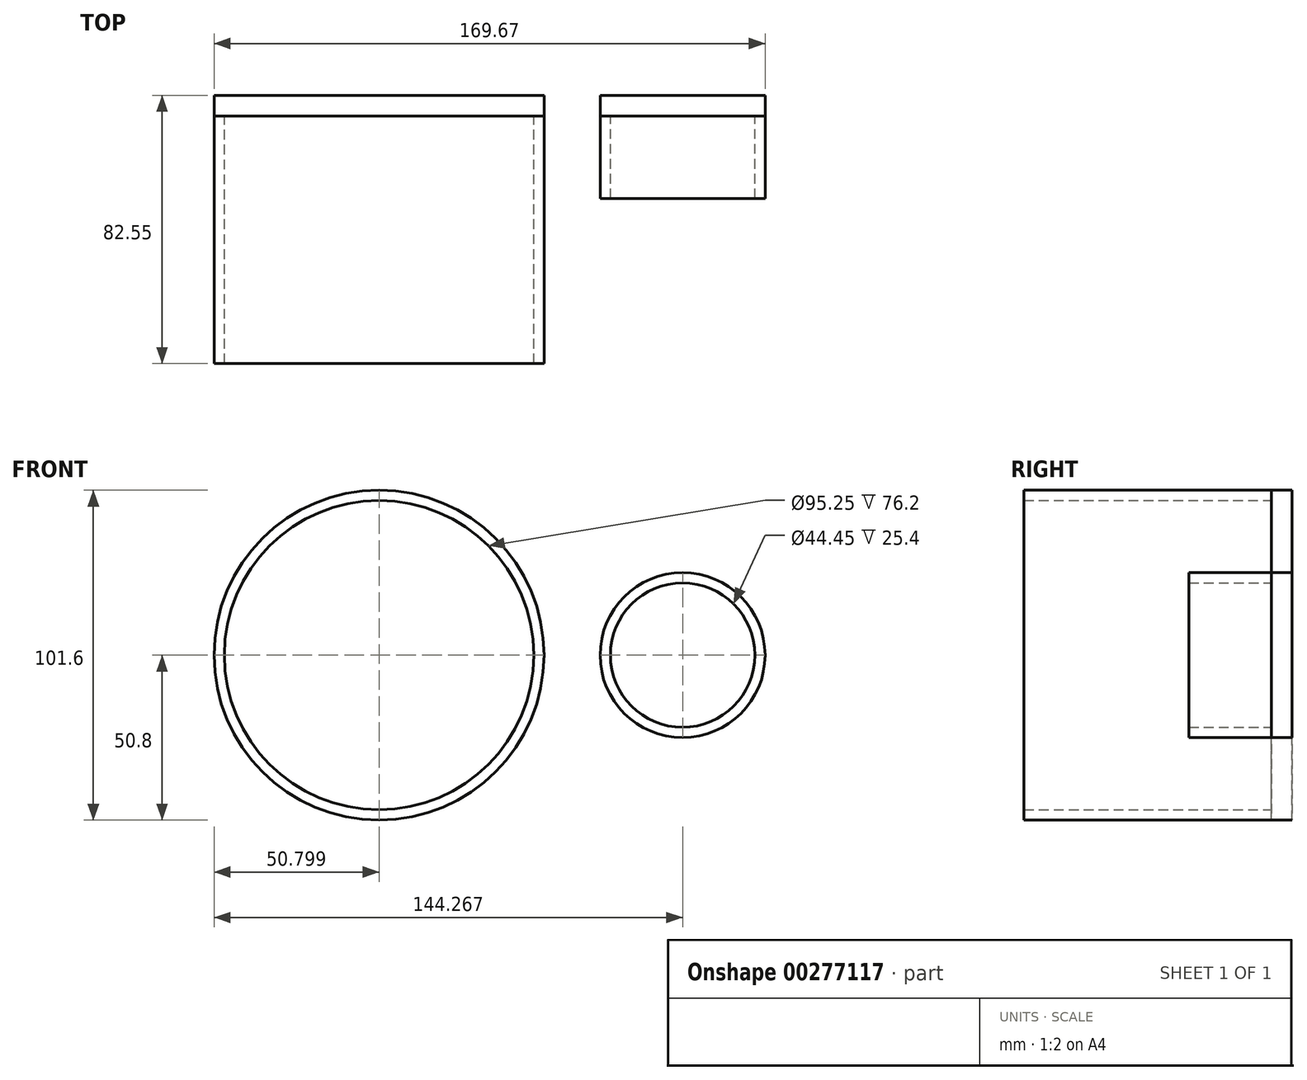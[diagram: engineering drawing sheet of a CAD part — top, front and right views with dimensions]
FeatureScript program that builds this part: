
annotation { "Feature Type Name" : "Feature", "Feature Type Description" : "" }
export const myFeature = defineFeature(function(context is Context, id is Id, definition is map)
    precondition{}
    {
        {
            var Q0;
            Q0=qCreatedBy(makeId("Front.planeOp"),FACE);
            var sketch = newSketch(context, id + "F0", { "sketchPlane" : qUnion([Q0])});
            skCircle(sketch, "E0", {"center": v(-48.3, 0) * mm, "radius": 47.63 * mm});
            skCircle(sketch, "E1", {"center": v(-48.3, 0) * mm, "radius": 50.8 * mm});
            skCircle(sketch, "E2", {"center": v(45.17, 0) * mm, "radius": 25.4 * mm});
            skCircle(sketch, "E3", {"center": v(45.17, 0) * mm, "radius": 22.23 * mm});
            skSolve(sketch);
        }
        {
            var Q0;
            Q0=makeQuery(id+"F0.imprint","IMPRINT",FACE,{"disambiguationData":[TD([[makeQuery(id+"F0.imprint","IMPRINT",EDGE,{"derivedFrom":sQuery(id+"F0.wireOp",EDGE,"E0")}),-1.0]])]});
            var Q1;
            Q1=makeQuery(id+"F0.imprint","IMPRINT",FACE,{"disambiguationData":[TD([[makeQuery(id+"F0.imprint","IMPRINT",EDGE,{"derivedFrom":sQuery(id+"F0.wireOp",EDGE,"E0")}),1.0]])]});
            var Q2;
            Q2=makeQuery(id+"F0.imprint","IMPRINT",FACE,{"disambiguationData":[TD([[makeQuery(id+"F0.imprint","IMPRINT",EDGE,{"derivedFrom":sQuery(id+"F0.wireOp",EDGE,"E3")}),1.0]])]});
            var Q3;
            Q3=makeQuery(id+"F0.imprint","IMPRINT",FACE,{"disambiguationData":[TD([[makeQuery(id+"F0.imprint","IMPRINT",EDGE,{"derivedFrom":sQuery(id+"F0.wireOp",EDGE,"E2")}),1.0]])]});
            extrude(context, id + "F1", {"entities" : qUnion([Q0, Q1, Q2, Q3]), "oppositeDirection" : true, "depth" : 6.35 * mm});
        }
        {
            var Q0;
            Q0=makeQuery(id+"F0.imprint","IMPRINT",FACE,{"disambiguationData":[TD([[makeQuery(id+"F0.imprint","IMPRINT",EDGE,{"derivedFrom":sQuery(id+"F0.wireOp",EDGE,"E0")}),-1.0]])]});
            extrude(context, id + "F2", {"entities" : qUnion([Q0]), "depth" : 76.2 * mm});
        }
        {
            var Q0;
            Q0=makeQuery(id+"F0.imprint","IMPRINT",FACE,{"disambiguationData":[TD([[makeQuery(id+"F0.imprint","IMPRINT",EDGE,{"derivedFrom":sQuery(id+"F0.wireOp",EDGE,"E2")}),1.0]])]});
            extrude(context, id + "F3", {"entities" : qUnion([Q0]), "depth" : 25.4 * mm});
        }
    });
